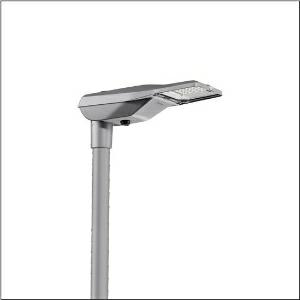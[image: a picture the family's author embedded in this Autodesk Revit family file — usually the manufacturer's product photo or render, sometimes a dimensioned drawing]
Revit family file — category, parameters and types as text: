
# Revit family: streetlight_sl_21_iq_micro___p0_5a_5xe1v31u08cb_845f
name_source: partatom
category: Lighting Fixtures
units: mm (PartAtom-declared; Revit-internal decimal feet)

## family parameters
Cut with Voids When Loaded = No
Host = Face
Light Source = No
Part Type = Normal
Room Calculation Point = No
Round Connector Dimension = Use Diameter
Shared = No

## types (1)
- --- (1 x LED, 2840 lm, 19.1 W, 3000K)
    Apparent Load = 19 VA
    CIE Flux Codes = 37 73 96 100 100
    Color Rendering = 70
    Color Temperature = 3000K
    Default Elevation = 1800 mm
    Description = Streetlight SL 21 iQ micro, mast luminaire, primary light control with lens, of PMMA, primary optical cover: cover, of toughened safety glass, transparent, light distribution: P0.5a, light emission: direct distribution, primary light characteristic: asymmetric, installation type: post-top, side-entry, LED, High Power LED, rated luminous flux: 2.840lm, luminous efficacy: 149lm/W, light colour: 730, colour temperature: 3000K, control gear: iQ-Street Remote, D4i with power reduction, control: pre-setting: logarithmic dimming characteristic, Street-Remote, Auto-Match, Temp-Guard, Lumen-Switch, Night-Set, Smart-Wire, Light-Fading, Desk-Remote (wireless, voltage-free reading and setting of iQ features in the workshop via application-optimized NFC function/RFID function), optimised constant luminous flux control (CLO 2.0), mains connection: 220..240V, AC, 50/60Hz, start of lifetime: 19W, end of service life: 20W, reduction: 9W, luminaire housing, of diecast aluminium, powder-coated, Siteco® metallic grey (DB 702S), corrosivity category C5 mid according to DIN EN ISO 12944, please order mast flange separately, inclination adjustable: 0°, 5°, 10°, 15°, sealing non-destructively replaceable, multi-level sealing system, length: 528mm, width: 235mm, height: 110mm, mast flange for spigot size: 42mm (side-entry): 5XC10008XM4, 60/48mm (side-entry/post-top): 5XC10108XM2, 76/60mm (side-entry/post-top): 5XC10108XM1, mounting height: 4..8m, Smart Interface below, protection rating (complete): IP66, insulation class (complete): insulation class II (safety insulation), certification: CE, ENEC, ENEC+, VDE, impact resistance: IK10, permissible operating ambient temperature for outdoor applications: -40..+50°C, standard-compliant lighting for roads and squares, packaging unit: 1 piece

Light Distribution: P0.5a
    Height = 110 mm
    Lamp = 1 x LED
    Lamp Light Flux = 2840 lm
    Lamp Power = 19.1 W
    Lamp count = 1
    Length = 528 mm
    Luminous efficacy = 149 lm/W
    Manufacturer = Siteco
    ModVariant = No
    Model = 5XE1V31U08CB
    Number of Poles = 1
    OnlyDefault = Yes
    Power Factor = 1
    Product Name = Streetlight SL 21 iQ micro | P0.5a
    Product group = mast luminaire | pylon top
    ProductGroupID = 6100
    Protection Class = Protection class II
    Protection Degree = IP 66
    RLX_Detail_Level = 1
    RLX_Emergency_Light_Flux = 0 lm
    RLX_Emergency_Type = 0
    RLX_Emergency_Type_DB = No
    RlxData = <blob elided: 98709 chars, md5=8aad5f55>
    Socket = socket
    Standby Power = 0 W
    System Light Flux = 2840 lm
    System Power = 19 W
    Type Comments = factory setting: luminous flux: 100 % | dim-lin: 254 | 387 mA
    Type Image = l_1277290.jpg
    URL = http://relux.com
    VarID = @adj_070256
    Voltage = 0 V
    Weight = 0.00 kg
    Width = 235 mm

## geometry (parser evidence)
native form markers: Blend x4, Sweep x11
no freeform markers — native parametric forms only
